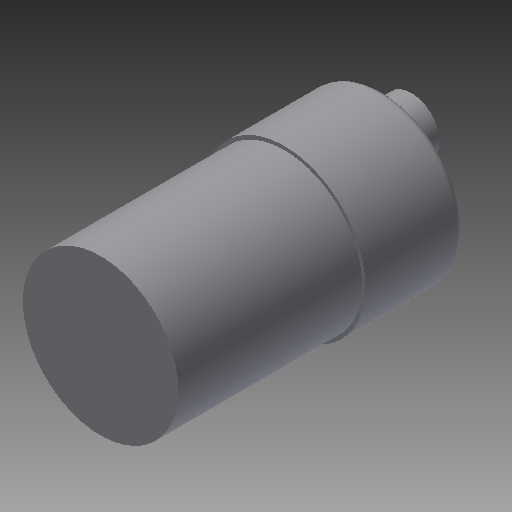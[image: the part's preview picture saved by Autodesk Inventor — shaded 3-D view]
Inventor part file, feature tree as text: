
AUTODESK INVENTOR PART (.ipt)
format: ipt  version: 2017 (Build 210142000, 142)  size: 130,048 bytes
history: native  units: in
note: dims shown in document units (in); Inventor stores cm internally (conversion verified against a paired STEP export)
features: sketch x4, extrude x3, fillet x1, hole x1
ambient origin geometry x8: Origin, YZ Plane, XZ Plane, XY Plane, X Axis, Y Axis, Z Axis, Center Point
bodies: Solid1 (feature_tree)
feature tree (9):
  extrude  "Extrusion1"  Depth=0.875in TaperAngle=0.0deg
  extrude  "Extrusion2"  Depth=1.625in TaperAngle=0.0deg
  fillet  "Fillet1"  Radius=0.0625in
  extrude  "Extrusion3"  Depth=0.3125in
  hole  "Hole1"  [1 undecoded]
  sketch  "Sketch1"  dims[d0=1.4375in d1=0.875in d2=0.0in]
  sketch  "Sketch2"  dims[d3=1.375in d4=1.625in d5=0.0in d6=0.0625in]
  sketch  "Sketch3"  dims[d7=0.5in d8=0.3125in]
  sketch  "Sketch4"  dims[d9=0.25in d10=0.0in d11=0.25in d12=0.25in d13=0.75in d14=0.375in d15=0.25in d16=0.5635in d17=0.25in d18=0.0in d19=1.0in d20=1.0in]
note: 1 required parameter value undecoded (feature->parameter linkage not recoverable at this tier; creation-order binding heuristic only, values carry confidence <= 0.55)
